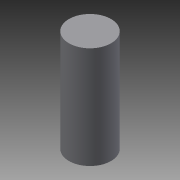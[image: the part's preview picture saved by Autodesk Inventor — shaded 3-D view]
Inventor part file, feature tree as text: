
AUTODESK INVENTOR PART (.ipt)
format: ipt  version: 2015 (Build 190159000, 159)  size: 82,432 bytes
history: native  units: mm
features: extrude x1, sketch x1
ambient origin geometry x8: Origin, YZ Plane, XZ Plane, XY Plane, X Axis, Y Axis, Z Axis, Center Point
bodies: Solid1 (feature_tree)
feature tree (2):
  extrude  "Extrusion1"  TaperAngle=0.0deg  [1 undecoded]
  sketch  "Sketch1"  dims[d2=0.0mm d3=0.0mm d4=0.0mm d9=0.0mm d10=0.0mm]
note: 1 required parameter value undecoded (feature->parameter linkage not recoverable at this tier; creation-order binding heuristic only, values carry confidence <= 0.55)
